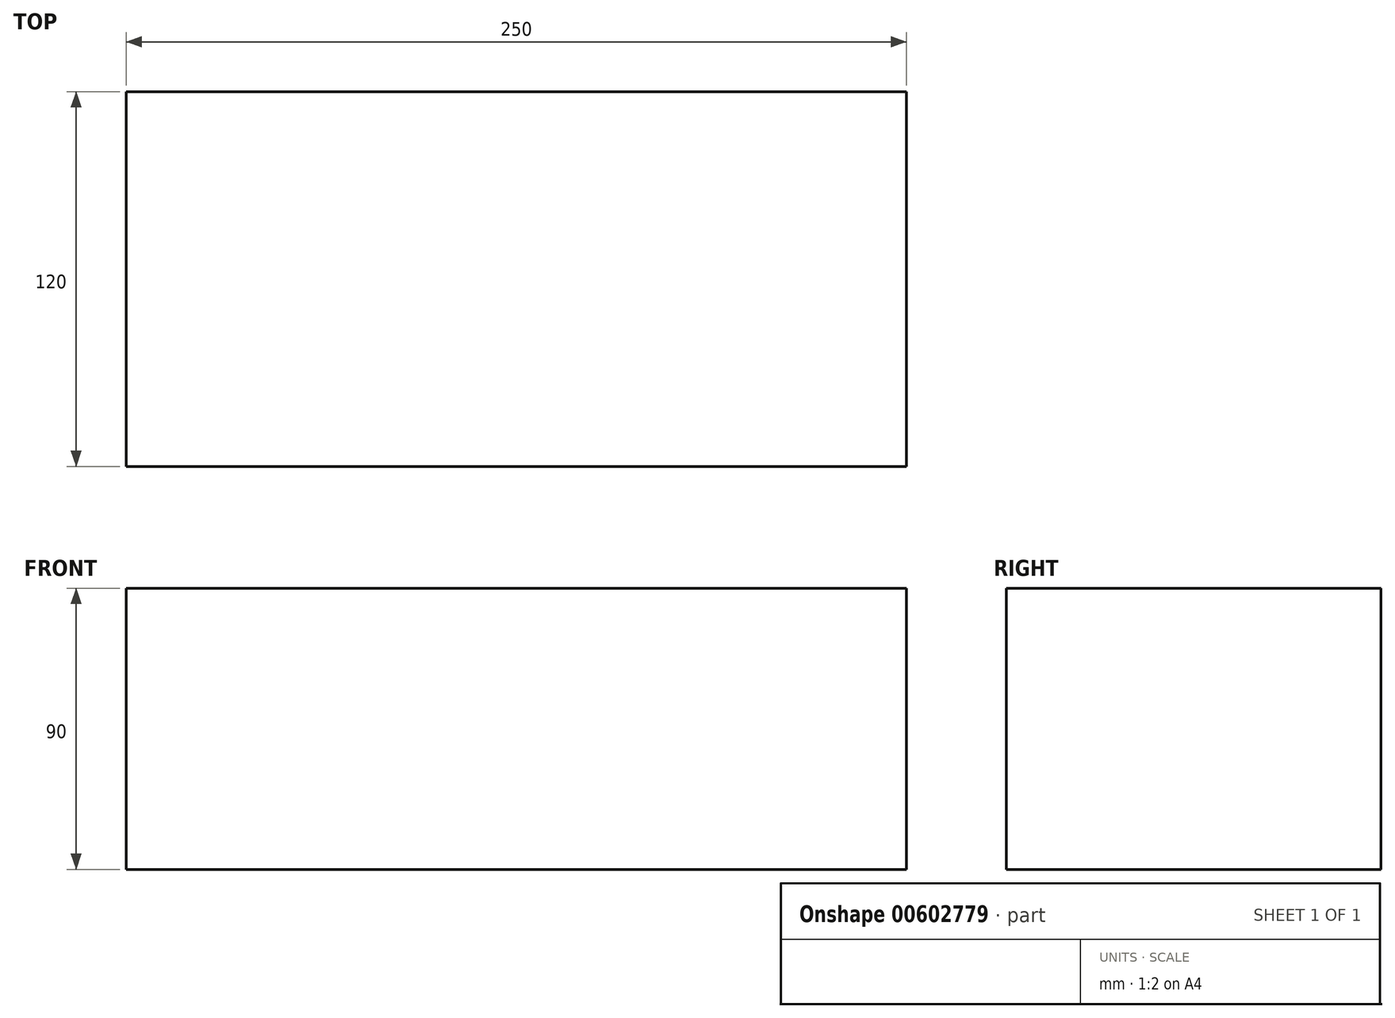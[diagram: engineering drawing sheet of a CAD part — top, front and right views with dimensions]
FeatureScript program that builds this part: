
annotation { "Feature Type Name" : "Feature", "Feature Type Description" : "" }
export const myFeature = defineFeature(function(context is Context, id is Id, definition is map)
    precondition{}
    {
        {
            var Q0;
            Q0=qCreatedBy(makeId("Top.planeOp"),FACE);
            var sketch = newSketch(context, id + "F0", { "sketchPlane" : qUnion([Q0])});
            skLineSegment(sketch, "E0.bottom", {"start": v(0, 0) * mm, "end": v(250, 0) * mm});
            skLineSegment(sketch, "E0.top", {"start": v(0, 120) * mm, "end": v(250, 120) * mm});
            skLineSegment(sketch, "E0.left", {"start": v(0, 0) * mm, "end": v(0, 120) * mm});
            skLineSegment(sketch, "E0.right", {"start": v(250, 0) * mm, "end": v(250, 120) * mm});
            skSolve(sketch);
        }
        {
            var Q0;
            Q0=makeQuery(id+"F0.imprint","IMPRINT",FACE,{"disambiguationData":[TD([[makeQuery(id+"F0.imprint","IMPRINT",EDGE,{"derivedFrom":sQuery(id+"F0.wireOp",EDGE,"E0.bottom")}),1.0]])]});
            extrude(context, id + "F1", {"entities" : qUnion([Q0]), "depth" : 90 * mm, "offsetDistance" : 25 * mm});
        }
    });
